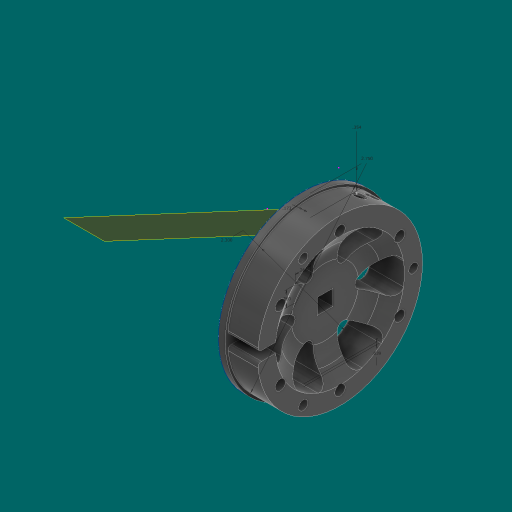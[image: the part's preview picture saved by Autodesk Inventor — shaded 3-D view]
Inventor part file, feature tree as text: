
AUTODESK INVENTOR PART (.ipt)
format: ipt  version: 2023.1 (Build 271208000, 208)  size: 1,231,360 bytes
history: native  units: in
note: dims shown in document units (in); Inventor stores cm internally (conversion verified against a paired STEP export)
features: extrude x8, sketch x7, fillet x5, other x5, pattern_circular x3, chamfer x3, revolve x1, plane x1
ambient origin geometry x8: Origin, YZ Plane, XZ Plane, XY Plane, X Axis, Y Axis, Z Axis, Center Point
bodies: Solid1 (feature_tree)
feature tree (33):
  sketch  "Sketch1"  dims[d0=2.75in d1=0.0394in]
  extrude  "Extrusion1"  Depth=0.0394in
  extrude  "Extrusion2"  Depth=0.5in TaperAngle=0.0deg
  extrude  "Extrusion3"  Depth=0.875in
  revolve  "Revolution1"  [1 undecoded]
  fillet  "Fillet5"  Radius=2.3622in
  sketch  "Sketch4"  dims[d9=0.3in d10=0.4in d11=2.3622in d13=360.0deg]
  extrude  "Extrusion4"  TaperAngle=45.0deg  [1 undecoded]
  extrude  "Extrusion5"  Depth=0.5in
  pattern_circular  "Circular Pattern4"  [2 undecoded]
  fillet  "Fillet7"  [1 undecoded]
  extrude  "Extrusion6"  Depth=0.0236in
  chamfer  "Chamfer1"  Distance=0.3543in
  fillet  "Fillet8"  Radius=0.1732in
  fillet  "Fillet9"  Radius=0.2431in
  pattern_circular  "Circular Pattern5"  [2 undecoded]
  extrude  "Extrusion8"  Depth=2.3622in TaperAngle=360.0deg
  chamfer  "Chamfer3"  Distance=0.0394in
  fillet  "Fillet10"  Radius=0.8937in
  plane  "Work Plane1"
  extrude  "Extrusion9"  Depth=0.1in
  chamfer  "Chamfer4"  Distance=0.1562in
  pattern_circular  "Circular Pattern7"  Count=3 Angle=360.0deg
  sketch  "Sketch2"  dims[d3=0.1181in d4=0.0in d5=0.5in d6=0.0in]
  sketch  "Sketch3"  dims[d7=0.875in d8=0.875in]
  sketch  "Sketch5"  dims[d15=0.0in d16=0.0in d17=45.0deg]
  sketch  "Sketch6"  dims[d18=0.0787in d19=0.5in]
  sketch  "Sketch7"  dims[d21=0.2405in d23=0.25in d24=360.0deg d35=0.0236in d41=0.3543in d42=0.1732in d43=0.2431in d44=0.0in d45=0.0in d46=0.0in d47=2.3622in d48=360.0deg d50=0.0394in d51=0.8937in d52=0.1in d53=0.1562in d55=1.1811in d57=360.0deg d59=0.2431in d60=0.0in d61=0.0472in d62=0.125in d63=45.0deg d67=0.26in d68=0.26in d69=2.3in d71=0.1in d72=0.125in d73=2.3622in d74=360.0deg d88=0.0591in d89=0.0787in d90=1.0in d91=0.0in d92=0.0472in d93=0.125in d94=45.0deg d95=0.5in d96=2.45in d97=0.1562in d98=1.0in d99=0.0in d100=0.0236in d101=0.125in d102=45.0deg d103=0.4466in d107=0.7874in d108=-0.0687in]
  other  "Work Axis1"
  other  "<userpath>\Documents\CAD\guardSwerve5\MainAssy.iam"
  other  "MainAssy.iam"
  other  "Bevel Gears:1"
  other  "Bevel Gear2:1"
note: 7 required parameter values undecoded (feature->parameter linkage not recoverable at this tier; creation-order binding heuristic only, values carry confidence <= 0.55)